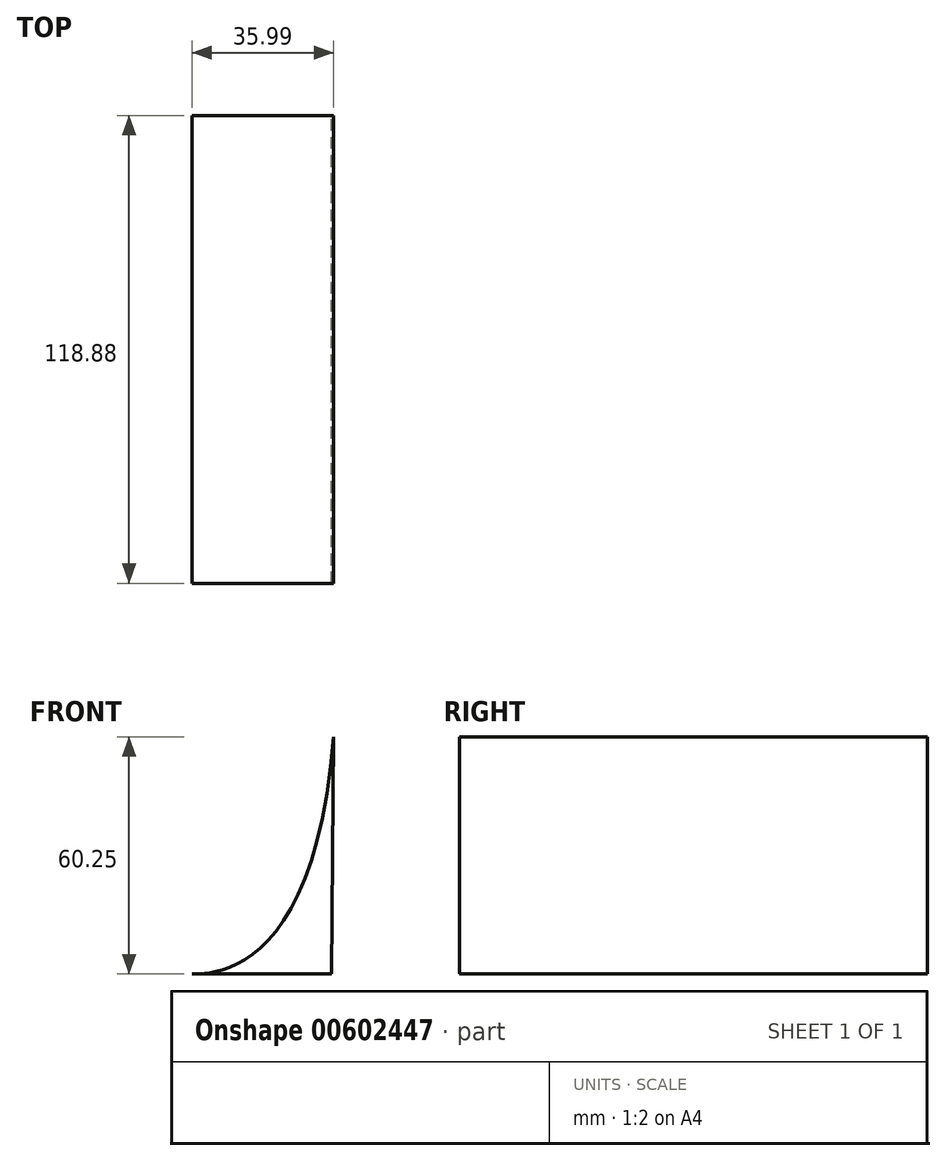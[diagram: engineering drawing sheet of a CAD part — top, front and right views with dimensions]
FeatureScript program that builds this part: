
annotation { "Feature Type Name" : "Feature", "Feature Type Description" : "" }
export const myFeature = defineFeature(function(context is Context, id is Id, definition is map)
    precondition{}
    {
        {
            var Q0;
            Q0=qCreatedBy(makeId("Front.planeOp"),FACE);
            var sketch = newSketch(context, id + "F0", { "sketchPlane" : qUnion([Q0])});
            skLineSegment(sketch, "E0", {"start": v(-75.89, 0) * mm, "end": v(76.75, 0) * mm});
            skLineSegment(sketch, "E1", {"start": v(0, 77.62) * mm, "end": v(0, -75.02) * mm});
            skFitSpline(sketch, "E2", {"points": [v(0, 0) * mm, v(36.75, 76.32) * mm], "startDerivative": vector(18.92, 0) * mm, "endDerivative": vector(3.91, 228.96) * mm});
            skLineSegment(sketch, "E3", {"start": v(36, 60.25) * mm, "end": v(35.44, 0) * mm});
            skSolve(sketch);
        }
        {
            var Q0;
            {var subQ3=sQuery(id+"F0.wireOp",EDGE,"E3");Q0=makeQuery(id+"F0.imprint","IMPRINT",FACE,{"disambiguationData":[TD([[makeQuery(id+"F0.imprint","IMPRINT",EDGE,{"derivedFrom":subQ3}),-1.0]])]});}
            extrude(context, id + "F1", {"entities" : qUnion([Q0]), "endBound" : BoundingType.SYMMETRIC, "depth" : 118.87 * mm, "offsetDistance" : 25.4 * mm});
        }
    });
